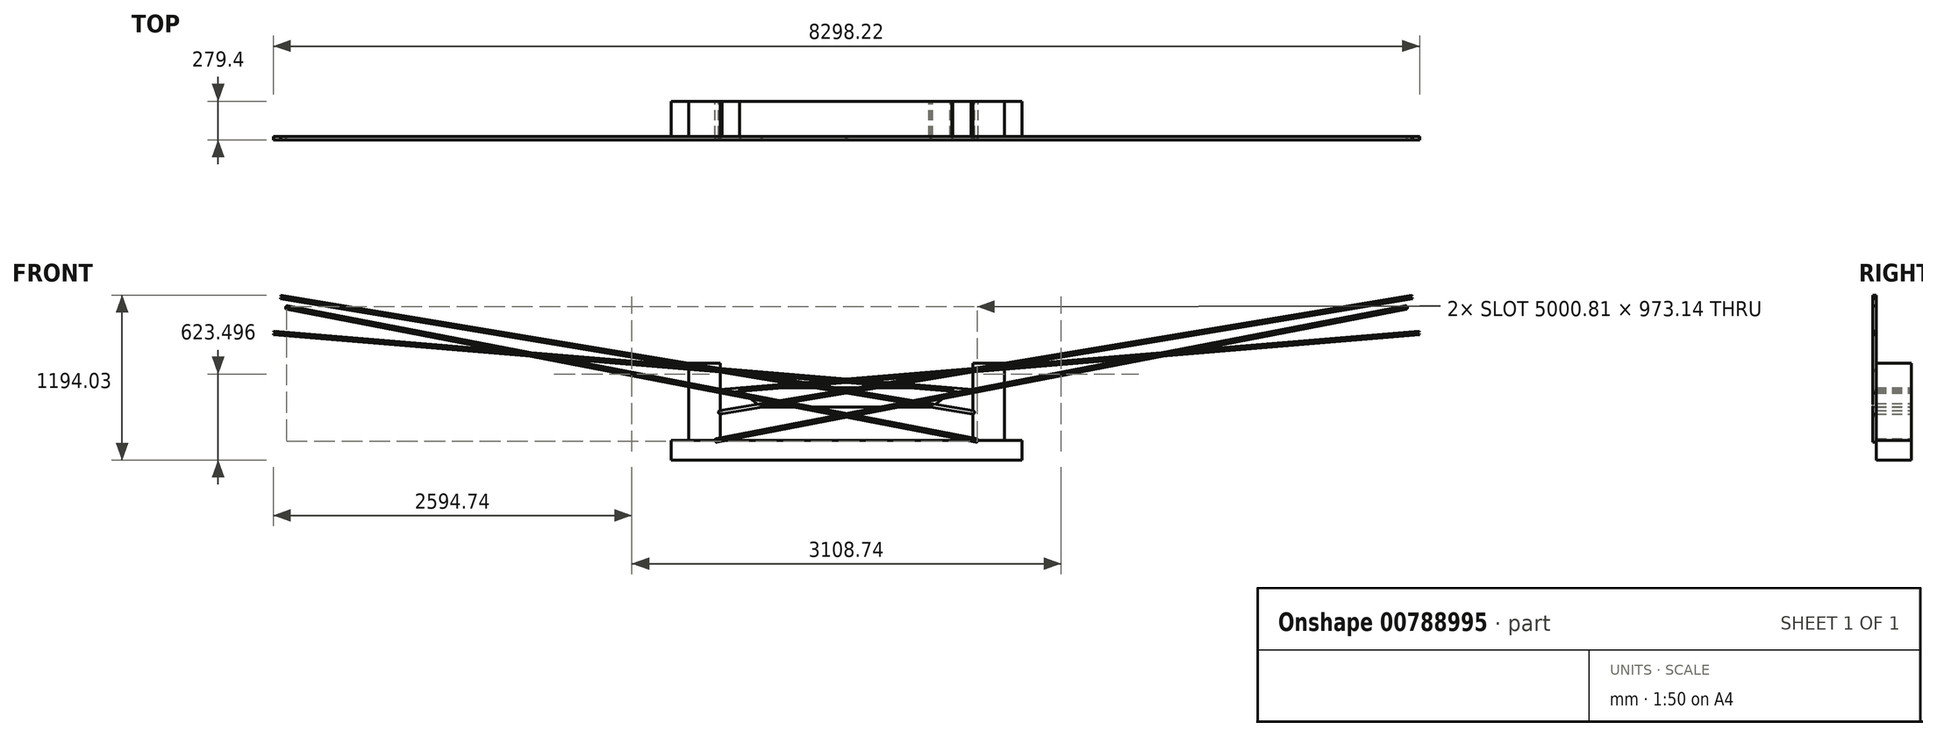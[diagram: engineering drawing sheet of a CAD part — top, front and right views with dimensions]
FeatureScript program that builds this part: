
annotation { "Feature Type Name" : "Feature", "Feature Type Description" : "" }
export const myFeature = defineFeature(function(context is Context, id is Id, definition is map)
    precondition{}
    {
        {
            var Q0;
            Q0=qCreatedBy(makeId("Front.planeOp"),FACE);
            var sketch = newSketch(context, id + "F0", { "sketchPlane" : qUnion([Q0])});
            skLineSegment(sketch, "E0.bottom", {"start": v(-914.4, 0) * mm, "end": v(-1143, 0) * mm});
            skLineSegment(sketch, "E0.top", {"start": v(-914.4, 558.8) * mm, "end": v(-1143, 558.8) * mm});
            skLineSegment(sketch, "E0.left", {"start": v(-914.4, 0) * mm, "end": v(-914.4, 558.8) * mm});
            skLineSegment(sketch, "E0.right", {"start": v(-1143, 0) * mm, "end": v(-1143, 558.8) * mm});
            skLineSegment(sketch, "E1.bottom", {"start": v(914.4, 0) * mm, "end": v(1143, 0) * mm});
            skLineSegment(sketch, "E1.top", {"start": v(914.4, 558.8) * mm, "end": v(1143, 558.8) * mm});
            skLineSegment(sketch, "E1.left", {"start": v(914.4, 0) * mm, "end": v(914.4, 558.8) * mm});
            skLineSegment(sketch, "E1.right", {"start": v(1143, 0) * mm, "end": v(1143, 558.8) * mm});
            skLineSegment(sketch, "E2", {"start": v(0, 0) * mm, "end": v(914.4, 0) * mm});
            skLineSegment(sketch, "E3", {"start": v(0, 0) * mm, "end": v(-914.4, 0) * mm});
            skLineSegment(sketch, "E4", {"start": v(-914.4, 279.4) * mm, "end": v(914.4, 279.4) * mm});
            skLineSegment(sketch, "E5", {"start": v(-762, 279.4) * mm, "end": v(-762, 368.3) * mm});
            skLineSegment(sketch, "E6", {"start": v(-609.6, 279.4) * mm, "end": v(-609.6, 254) * mm});
            skLineSegment(sketch, "E7", {"start": v(-914.4, 279.4) * mm, "end": v(-914.4, 355.6) * mm});
            skLineSegment(sketch, "E8", {"start": v(-914.4, 279.4) * mm, "end": v(-914.4, 203.2) * mm});
            skCircle(sketch, "E9", {"center": v(-914.4, 355.6) * mm, "radius": 12.7 * mm});
            skCircle(sketch, "E10", {"center": v(-914.4, 203.2) * mm, "radius": 12.7 * mm});
            skCircle(sketch, "E11", {"center": v(-762, 368.3) * mm, "radius": 12.7 * mm});
            skCircle(sketch, "E12", {"center": v(-609.6, 254) * mm, "radius": 12.7 * mm});
            skLineSegment(sketch, "E13", {"start": v(-762, 381) * mm, "end": v(0, 381) * mm});
            skLineSegment(sketch, "E14", {"start": v(0, 381) * mm, "end": v(0, 241.3) * mm});
            skLineSegment(sketch, "E15", {"start": v(0, 241.3) * mm, "end": v(-609.6, 241.3) * mm});
            skLineSegment(sketch, "E16", {"start": v(-769.62, 358.14) * mm, "end": v(-617.22, 243.84) * mm});
            skLineSegment(sketch, "E17.MirrorCS", {"start": v(0, 241.3) * mm, "end": v(609.6, 241.3) * mm});
            skCircle(sketch, "E18.MirrorC", {"center": v(609.6, 254) * mm, "radius": 12.7 * mm});
            skLineSegment(sketch, "E19.MirrorCS", {"start": v(769.62, 358.14) * mm, "end": v(617.22, 243.84) * mm});
            skLineSegment(sketch, "E20.MirrorCS", {"start": v(762, 381) * mm, "end": v(0, 381) * mm});
            skCircle(sketch, "E21.MirrorC", {"center": v(762, 368.3) * mm, "radius": 12.7 * mm});
            skCircle(sketch, "E22.MirrorC", {"center": v(914.4, 203.2) * mm, "radius": 12.7 * mm});
            skCircle(sketch, "E23.MirrorC", {"center": v(914.4, 355.6) * mm, "radius": 12.7 * mm});
            skCircle(sketch, "E24", {"center": v(-939.8, 0) * mm, "radius": 12.7 * mm});
            skCircle(sketch, "E25.MirrorC", {"center": v(939.8, 0) * mm, "radius": 12.7 * mm});
            skSolve(sketch);
        }
        {
            var Q0;
            {var subQ1=sQuery(id+"F0.wireOp",EDGE,"E0.bottom");Q0=makeQuery(id+"F0.imprint","IMPRINT",FACE,{"disambiguationData":[TD([[makeQuery(id+"F0.imprint","IMPRINT",EDGE,{"derivedFrom":subQ1}),-1.0]])]});}
            var Q1;
            {var subQ0=sQuery(id+"F0.wireOp",EDGE,"E7");var subQ1=sQuery(id+"F0.wireOp",EDGE,"E0.left");var subQ2=makeQuery(id+"F0.imprint","INTERSECT",VERTEX,{"derivedFrom":[subQ1,subQ0]});Q1=makeQuery(id+"F0.imprint","IMPRINT",FACE,{"disambiguationData":[TD([[makeQuery(id+"F0.imprint","IMPRINT",EDGE,{"disambiguationData":[TD([[subQ2,-1.0]])],"derivedFrom":subQ1}),-1.0]])]});}
            var Q2;
            {var subQ0=sQuery(id+"F0.wireOp",EDGE,"E7");var subQ1=sQuery(id+"F0.wireOp",EDGE,"E0.left");var subQ2=makeQuery(id+"F0.imprint","INTERSECT",VERTEX,{"derivedFrom":[subQ1,subQ0]});Q2=makeQuery(id+"F0.imprint","IMPRINT",FACE,{"disambiguationData":[TD([[makeQuery(id+"F0.imprint","IMPRINT",EDGE,{"disambiguationData":[TD([[subQ2,-1.0]])],"derivedFrom":subQ1}),1.0]])]});}
            var Q3;
            {var subQ0=sQuery(id+"F0.wireOp",EDGE,"E11");var subQ1=makeQuery(id+"F0.imprint","INTERSECT",VERTEX,{"derivedFrom":[subQ0,sQuery(id+"F0.wireOp",EDGE,"E13")]});Q3=makeQuery(id+"F0.imprint","IMPRINT",FACE,{"disambiguationData":[TD([[makeQuery(id+"F0.imprint","IMPRINT",EDGE,{"disambiguationData":[TD([[subQ1,-1.0]])],"derivedFrom":subQ0}),1.0]])]});}
            var Q4;
            {var subQ0=sQuery(id+"F0.wireOp",EDGE,"E13");Q4=makeQuery(id+"F0.imprint","IMPRINT",FACE,{"disambiguationData":[TD([[makeQuery(id+"F0.imprint","IMPRINT",EDGE,{"derivedFrom":subQ0}),-1.0]])]});}
            var Q5;
            {var subQ0=sQuery(id+"F0.wireOp",EDGE,"E16");var subQ1=sQuery(id+"F0.wireOp",EDGE,"E5");var subQ2=makeQuery(id+"F0.imprint","INTERSECT",VERTEX,{"derivedFrom":[subQ1,subQ0]});Q5=makeQuery(id+"F0.imprint","IMPRINT",FACE,{"disambiguationData":[TD([[makeQuery(id+"F0.imprint","IMPRINT",EDGE,{"disambiguationData":[TD([[subQ2,-1.0]])],"derivedFrom":subQ1}),1.0]])]});}
            var Q6;
            {var subQ0=sQuery(id+"F0.wireOp",EDGE,"E8");var subQ1=sQuery(id+"F0.wireOp",EDGE,"E0.left");var subQ2=makeQuery(id+"F0.imprint","INTERSECT",VERTEX,{"derivedFrom":[subQ1,subQ0]});Q6=makeQuery(id+"F0.imprint","IMPRINT",FACE,{"disambiguationData":[TD([[makeQuery(id+"F0.imprint","IMPRINT",EDGE,{"disambiguationData":[TD([[subQ2,1.0]])],"derivedFrom":subQ1}),1.0]])]});}
            var Q7;
            {var subQ0=sQuery(id+"F0.wireOp",EDGE,"E8");var subQ1=sQuery(id+"F0.wireOp",EDGE,"E0.left");var subQ2=makeQuery(id+"F0.imprint","INTERSECT",VERTEX,{"derivedFrom":[subQ1,subQ0]});Q7=makeQuery(id+"F0.imprint","IMPRINT",FACE,{"disambiguationData":[TD([[makeQuery(id+"F0.imprint","IMPRINT",EDGE,{"disambiguationData":[TD([[subQ2,1.0]])],"derivedFrom":subQ1}),-1.0]])]});}
            var Q8;
            {var subQ0=sQuery(id+"F0.wireOp",EDGE,"E6");var subQ1=sQuery(id+"F0.wireOp",EDGE,"E4");var subQ2=makeQuery(id+"F0.imprint","INTERSECT",VERTEX,{"derivedFrom":[subQ1,subQ0]});Q8=makeQuery(id+"F0.imprint","IMPRINT",FACE,{"disambiguationData":[TD([[makeQuery(id+"F0.imprint","IMPRINT",EDGE,{"disambiguationData":[TD([[subQ2,1.0]])],"derivedFrom":subQ1}),-1.0]])]});}
            var Q9;
            {var subQ0=sQuery(id+"F0.wireOp",EDGE,"E12");var subQ1=makeQuery(id+"F0.imprint","INTERSECT",VERTEX,{"derivedFrom":[subQ0,sQuery(id+"F0.wireOp",EDGE,"E16")]});Q9=makeQuery(id+"F0.imprint","IMPRINT",FACE,{"disambiguationData":[TD([[makeQuery(id+"F0.imprint","IMPRINT",EDGE,{"disambiguationData":[TD([[subQ1,1.0]])],"derivedFrom":subQ0}),1.0]])]});}
            var Q10;
            {var subQ0=sQuery(id+"F0.wireOp",EDGE,"E15");Q10=makeQuery(id+"F0.imprint","IMPRINT",FACE,{"disambiguationData":[TD([[makeQuery(id+"F0.imprint","IMPRINT",EDGE,{"derivedFrom":subQ0}),-1.0]])]});}
            var Q11;
            {var subQ1=sQuery(id+"F0.wireOp",EDGE,"E17.MirrorCS");Q11=makeQuery(id+"F0.imprint","IMPRINT",FACE,{"disambiguationData":[TD([[makeQuery(id+"F0.imprint","IMPRINT",EDGE,{"derivedFrom":subQ1}),1.0]])]});}
            var Q12;
            {var subQ0=sQuery(id+"F0.wireOp",EDGE,"E18.MirrorC");var subQ1=makeQuery(id+"F0.imprint","INTERSECT",VERTEX,{"derivedFrom":[sQuery(id+"F0.wireOp",EDGE,"E17.MirrorCS"),subQ0]});Q12=makeQuery(id+"F0.imprint","IMPRINT",FACE,{"disambiguationData":[TD([[makeQuery(id+"F0.imprint","IMPRINT",EDGE,{"disambiguationData":[TD([[subQ1,1.0]])],"derivedFrom":subQ0}),-1.0]])]});}
            var Q13;
            {var subQ0=sQuery(id+"F0.wireOp",EDGE,"E20.MirrorCS");Q13=makeQuery(id+"F0.imprint","IMPRINT",FACE,{"disambiguationData":[TD([[makeQuery(id+"F0.imprint","IMPRINT",EDGE,{"derivedFrom":subQ0}),1.0]])]});}
            var Q14;
            {var subQ0=sQuery(id+"F0.wireOp",EDGE,"E21.MirrorC");var subQ1=makeQuery(id+"F0.imprint","INTERSECT",VERTEX,{"derivedFrom":[sQuery(id+"F0.wireOp",EDGE,"E19.MirrorCS"),subQ0]});Q14=makeQuery(id+"F0.imprint","IMPRINT",FACE,{"disambiguationData":[TD([[makeQuery(id+"F0.imprint","IMPRINT",EDGE,{"disambiguationData":[TD([[subQ1,1.0]])],"derivedFrom":subQ0}),-1.0]])]});}
            var Q15;
            {var subQ0=sQuery(id+"F0.wireOp",EDGE,"E23.MirrorC");var subQ1=sQuery(id+"F0.wireOp",EDGE,"E1.left");var subQ2=makeQuery(id+"F0.imprint","INTERSECT",VERTEX,{"disambiguationData":[OD(0.0)],"derivedFrom":[subQ1,subQ0]});Q15=makeQuery(id+"F0.imprint","IMPRINT",FACE,{"disambiguationData":[TD([[makeQuery(id+"F0.imprint","IMPRINT",EDGE,{"disambiguationData":[TD([[subQ2,-1.0]])],"derivedFrom":subQ1}),-1.0]])]});}
            var Q16;
            {var subQ0=sQuery(id+"F0.wireOp",EDGE,"E23.MirrorC");var subQ1=sQuery(id+"F0.wireOp",EDGE,"E1.left");var subQ2=makeQuery(id+"F0.imprint","INTERSECT",VERTEX,{"disambiguationData":[OD(0.0)],"derivedFrom":[subQ1,subQ0]});Q16=makeQuery(id+"F0.imprint","IMPRINT",FACE,{"disambiguationData":[TD([[makeQuery(id+"F0.imprint","IMPRINT",EDGE,{"disambiguationData":[TD([[subQ2,-1.0]])],"derivedFrom":subQ1}),1.0]])]});}
            var Q17;
            {var subQ4=sQuery(id+"F0.wireOp",EDGE,"E1.bottom");Q17=makeQuery(id+"F0.imprint","IMPRINT",FACE,{"disambiguationData":[TD([[makeQuery(id+"F0.imprint","IMPRINT",EDGE,{"derivedFrom":subQ4}),1.0]])]});}
            var Q18;
            {var subQ0=sQuery(id+"F0.wireOp",EDGE,"E22.MirrorC");var subQ1=sQuery(id+"F0.wireOp",EDGE,"E1.left");var subQ2=makeQuery(id+"F0.imprint","INTERSECT",VERTEX,{"disambiguationData":[OD(0.0)],"derivedFrom":[subQ1,subQ0]});Q18=makeQuery(id+"F0.imprint","IMPRINT",FACE,{"disambiguationData":[TD([[makeQuery(id+"F0.imprint","IMPRINT",EDGE,{"disambiguationData":[TD([[subQ2,-1.0]])],"derivedFrom":subQ1}),-1.0]])]});}
            var Q19;
            {var subQ0=sQuery(id+"F0.wireOp",EDGE,"E22.MirrorC");var subQ1=sQuery(id+"F0.wireOp",EDGE,"E1.left");var subQ2=makeQuery(id+"F0.imprint","INTERSECT",VERTEX,{"disambiguationData":[OD(0.0)],"derivedFrom":[subQ1,subQ0]});Q19=makeQuery(id+"F0.imprint","IMPRINT",FACE,{"disambiguationData":[TD([[makeQuery(id+"F0.imprint","IMPRINT",EDGE,{"disambiguationData":[TD([[subQ2,-1.0]])],"derivedFrom":subQ1}),1.0]])]});}
            var Q20;
            {var subQ0=sQuery(id+"F0.wireOp",EDGE,"E24");var subQ1=sQuery(id+"F0.wireOp",EDGE,"E0.bottom");var subQ2=makeQuery(id+"F0.imprint","INTERSECT",VERTEX,{"disambiguationData":[OD(0.0)],"derivedFrom":[subQ1,subQ0]});Q20=makeQuery(id+"F0.imprint","IMPRINT",FACE,{"disambiguationData":[TD([[makeQuery(id+"F0.imprint","IMPRINT",EDGE,{"disambiguationData":[TD([[subQ2,-1.0]])],"derivedFrom":subQ1}),-1.0]])]});}
            var Q21;
            {var subQ0=sQuery(id+"F0.wireOp",EDGE,"E24");var subQ1=sQuery(id+"F0.wireOp",EDGE,"E0.bottom");var subQ2=makeQuery(id+"F0.imprint","INTERSECT",VERTEX,{"disambiguationData":[OD(0.0)],"derivedFrom":[subQ1,subQ0]});Q21=makeQuery(id+"F0.imprint","IMPRINT",FACE,{"disambiguationData":[TD([[makeQuery(id+"F0.imprint","IMPRINT",EDGE,{"disambiguationData":[TD([[subQ2,-1.0]])],"derivedFrom":subQ1}),1.0]])]});}
            var Q22;
            {var subQ0=sQuery(id+"F0.wireOp",EDGE,"E25.MirrorC");var subQ1=sQuery(id+"F0.wireOp",EDGE,"E1.bottom");var subQ2=makeQuery(id+"F0.imprint","INTERSECT",VERTEX,{"disambiguationData":[OD(0.0)],"derivedFrom":[subQ1,subQ0]});Q22=makeQuery(id+"F0.imprint","IMPRINT",FACE,{"disambiguationData":[TD([[makeQuery(id+"F0.imprint","IMPRINT",EDGE,{"disambiguationData":[TD([[subQ2,-1.0]])],"derivedFrom":subQ1}),1.0]])]});}
            var Q23;
            {var subQ0=sQuery(id+"F0.wireOp",EDGE,"E25.MirrorC");var subQ1=sQuery(id+"F0.wireOp",EDGE,"E1.bottom");var subQ2=makeQuery(id+"F0.imprint","INTERSECT",VERTEX,{"disambiguationData":[OD(0.0)],"derivedFrom":[subQ1,subQ0]});Q23=makeQuery(id+"F0.imprint","IMPRINT",FACE,{"disambiguationData":[TD([[makeQuery(id+"F0.imprint","IMPRINT",EDGE,{"disambiguationData":[TD([[subQ2,-1.0]])],"derivedFrom":subQ1}),-1.0]])]});}
            extrude(context, id + "F1", {"entities" : qUnion([Q0, Q1, Q2, Q3, Q4, Q5, Q6, Q7, Q8, Q9, Q10, Q11, Q12, Q13, Q14, Q15, Q16, Q17, Q18, Q19, Q20, Q21, Q22, Q23]), "depth" : 254 * mm, "offsetDistance" : 25.4 * mm});
        }
        {
            var Q0;
            Q0=makeQuery(id+"F1.opExtrude","CAP_FACE",FACE,{"disambiguationData":[OSD([sQuery(id+"F0.wireOp",EDGE,"E11"),sQuery(id+"F0.wireOp",EDGE,"E12"),sQuery(id+"F0.wireOp",EDGE,"E13"),sQuery(id+"F0.wireOp",EDGE,"E15"),sQuery(id+"F0.wireOp",EDGE,"E16"),sQuery(id+"F0.wireOp",EDGE,"E17.MirrorCS"),sQuery(id+"F0.wireOp",EDGE,"E18.MirrorC"),sQuery(id+"F0.wireOp",EDGE,"E19.MirrorCS"),sQuery(id+"F0.wireOp",EDGE,"E20.MirrorCS"),sQuery(id+"F0.wireOp",EDGE,"E21.MirrorC")])],"isStart":false});
            var sketch = newSketch(context, id + "F2", { "sketchPlane" : qUnion([Q0])});
            skCircle(sketch, "E26", {"center": v(-914.4, 355.6) * mm, "radius": 12.7 * mm});
            skCircle(sketch, "E27", {"center": v(-762, 368.3) * mm, "radius": 12.7 * mm});
            skLineSegment(sketch, "E28", {"start": v(-915.45, 368.26) * mm, "end": v(4147, 790.13) * mm});
            skLineSegment(sketch, "E29", {"start": v(4147, 790.13) * mm, "end": v(4149.1, 764.81) * mm});
            skLineSegment(sketch, "E30", {"start": v(4149.1, 764.81) * mm, "end": v(-913.35, 342.94) * mm});
            skArc(sketch, "E31", {"start": v(4147, 790.13) * mm, "mid": v(4160.7, 778.53) * mm, "end": v(4149.1, 764.81) * mm});
            skCircle(sketch, "E32", {"center": v(-762, 368.3) * mm, "radius": 6.35 * mm});
            skCircle(sketch, "E33", {"center": v(4148.05, 777.47) * mm, "radius": 6.35 * mm});
            skLineSegment(sketch, "E34", {"start": v(4148.58, 771.14) * mm, "end": v(-761.47, 361.97) * mm});
            skLineSegment(sketch, "E35", {"start": v(4147.53, 783.8) * mm, "end": v(-762.53, 374.63) * mm});
            skSolve(sketch);
        }
        {
            var Q0;
            {var subQ0=sQuery(id+"F2.wireOp",EDGE,"E28");var subQ1=sQuery(id+"F2.wireOp",EDGE,"E26");var subQ2=makeQuery(id+"F2.imprint","INTERSECT",VERTEX,{"derivedFrom":[subQ1,subQ0]});Q0=makeQuery(id+"F2.imprint","IMPRINT",FACE,{"disambiguationData":[TD([[makeQuery(id+"F2.imprint","IMPRINT",EDGE,{"disambiguationData":[TD([[subQ2,1.0]])],"derivedFrom":subQ1}),-1.0]])]});}
            var Q1;
            {var subQ0=sQuery(id+"F2.wireOp",EDGE,"E27");var subQ1=makeQuery(id+"F2.imprint","INTERSECT",VERTEX,{"derivedFrom":[makeQuery(id+"F1.opExtrude","CAP_EDGE",EDGE,{"disambiguationData":[OSD([sQuery(id+"F0.wireOp",EDGE,"E16")])],"isStart":false}),subQ0]});Q1=makeQuery(id+"F2.imprint","IMPRINT",FACE,{"disambiguationData":[TD([[makeQuery(id+"F2.imprint","IMPRINT",EDGE,{"disambiguationData":[TD([[subQ1,1.0]])],"derivedFrom":subQ0}),1.0]])]});}
            var Q2;
            {var subQ5=sQuery(id+"F2.wireOp",EDGE,"E27");var subQ7=sQuery(id+"F2.wireOp",EDGE,"E28");var subQ8=makeQuery(id+"F2.imprint","INTERSECT",VERTEX,{"derivedFrom":[subQ5,subQ7]});Q2=makeQuery(id+"F2.imprint","IMPRINT",FACE,{"disambiguationData":[TD([[makeQuery(id+"F2.imprint","IMPRINT",EDGE,{"disambiguationData":[TD([[subQ8,1.0]])],"derivedFrom":subQ5}),-1.0]])]});}
            var Q3;
            {var subQ0=sQuery(id+"F2.wireOp",EDGE,"E27");var subQ3=sQuery(id+"F2.wireOp",EDGE,"E35");var subQ4=makeQuery(id+"F2.imprint","INTERSECT",VERTEX,{"derivedFrom":[subQ0,subQ3]});Q3=makeQuery(id+"F2.imprint","IMPRINT",FACE,{"disambiguationData":[TD([[makeQuery(id+"F2.imprint","IMPRINT",EDGE,{"disambiguationData":[TD([[subQ4,-1.0]])],"derivedFrom":subQ0}),-1.0]])]});}
            var Q4;
            {var subQ0=sQuery(id+"F2.wireOp",EDGE,"E30");var subQ1=sQuery(id+"F2.wireOp",EDGE,"E27");var subQ2=makeQuery(id+"F2.imprint","INTERSECT",VERTEX,{"derivedFrom":[subQ1,subQ0]});Q4=makeQuery(id+"F2.imprint","IMPRINT",FACE,{"disambiguationData":[TD([[makeQuery(id+"F2.imprint","IMPRINT",EDGE,{"disambiguationData":[TD([[subQ2,-1.0]])],"derivedFrom":subQ1}),-1.0]])]});}
            var Q5;
            {var subQ0=sQuery(id+"F2.wireOp",EDGE,"E30");var subQ1=sQuery(id+"F2.wireOp",EDGE,"E29");var subQ2=makeQuery(id+"F2.imprint","INTERSECT",VERTEX,{"derivedFrom":[subQ1,subQ0,sQuery(id+"F2.wireOp",EDGE,"E31")]});Q5=makeQuery(id+"F2.imprint","IMPRINT",FACE,{"disambiguationData":[TD([[makeQuery(id+"F2.imprint","IMPRINT",EDGE,{"disambiguationData":[TD([[subQ2,1.0]])],"derivedFrom":subQ1}),-1.0]])]});}
            var Q6;
            {var subQ0=sQuery(id+"F2.wireOp",EDGE,"E31");Q6=makeQuery(id+"F2.imprint","IMPRINT",FACE,{"disambiguationData":[TD([[makeQuery(id+"F2.imprint","IMPRINT",EDGE,{"derivedFrom":subQ0}),-1.0]])]});}
            var Q7;
            {var subQ0=sQuery(id+"F2.wireOp",EDGE,"E26");var subQ1=makeQuery(id+"F2.imprint","INTERSECT",VERTEX,{"derivedFrom":[subQ0,sQuery(id+"F2.wireOp",EDGE,"E28")]});Q7=makeQuery(id+"F2.imprint","IMPRINT",FACE,{"disambiguationData":[TD([[makeQuery(id+"F2.imprint","IMPRINT",EDGE,{"disambiguationData":[TD([[subQ1,-1.0]])],"derivedFrom":subQ0}),1.0]])]});}
            extrude(context, id + "F3", {"entities" : qUnion([Q0, Q1, Q2, Q3, Q4, Q5, Q6, Q7]), "depth" : 25.4 * mm, "offsetDistance" : 25.4 * mm});
        }
        {
            var Q0;
            Q0=makeQuery(id+"F1.opExtrude","CAP_FACE",FACE,{"disambiguationData":[OSD([sQuery(id+"F0.wireOp",EDGE,"E11"),sQuery(id+"F0.wireOp",EDGE,"E12"),sQuery(id+"F0.wireOp",EDGE,"E13"),sQuery(id+"F0.wireOp",EDGE,"E15"),sQuery(id+"F0.wireOp",EDGE,"E16"),sQuery(id+"F0.wireOp",EDGE,"E17.MirrorCS"),sQuery(id+"F0.wireOp",EDGE,"E18.MirrorC"),sQuery(id+"F0.wireOp",EDGE,"E19.MirrorCS"),sQuery(id+"F0.wireOp",EDGE,"E20.MirrorCS"),sQuery(id+"F0.wireOp",EDGE,"E21.MirrorC")])],"isStart":false});
            var sketch = newSketch(context, id + "F4", { "sketchPlane" : qUnion([Q0])});
            skCircle(sketch, "E36", {"center": v(-914.4, 203.2) * mm, "radius": 12.7 * mm});
            skCircle(sketch, "E37", {"center": v(-609.6, 254) * mm, "radius": 12.7 * mm});
            skLineSegment(sketch, "E38", {"start": v(-916.49, 215.73) * mm, "end": v(4094.4, 1050.87) * mm});
            skLineSegment(sketch, "E39", {"start": v(4094.4, 1050.87) * mm, "end": v(4098.57, 1025.82) * mm});
            skLineSegment(sketch, "E40", {"start": v(4098.57, 1025.82) * mm, "end": v(-912.31, 190.67) * mm});
            skArc(sketch, "E41", {"start": v(4094.4, 1050.87) * mm, "mid": v(4109, 1040.43) * mm, "end": v(4098.57, 1025.82) * mm});
            skCircle(sketch, "E42", {"center": v(-609.6, 254) * mm, "radius": 6.35 * mm});
            skCircle(sketch, "E43", {"center": v(4096.48, 1038.35) * mm, "radius": 6.35 * mm});
            skLineSegment(sketch, "E44", {"start": v(4095.44, 1044.61) * mm, "end": v(-610.64, 260.26) * mm});
            skLineSegment(sketch, "E45", {"start": v(4097.53, 1032.08) * mm, "end": v(-608.56, 247.74) * mm});
            skSolve(sketch);
        }
        {
            var Q0;
            {var subQ0=sQuery(id+"F4.wireOp",EDGE,"E41");Q0=makeQuery(id+"F4.imprint","IMPRINT",FACE,{"disambiguationData":[TD([[makeQuery(id+"F4.imprint","IMPRINT",EDGE,{"derivedFrom":subQ0}),-1.0]])]});}
            var Q1;
            {var subQ0=sQuery(id+"F4.wireOp",EDGE,"E40");var subQ1=sQuery(id+"F4.wireOp",EDGE,"E37");var subQ2=makeQuery(id+"F4.imprint","INTERSECT",VERTEX,{"derivedFrom":[subQ1,subQ0]});Q1=makeQuery(id+"F4.imprint","IMPRINT",FACE,{"disambiguationData":[TD([[makeQuery(id+"F4.imprint","IMPRINT",EDGE,{"disambiguationData":[TD([[subQ2,-1.0]])],"derivedFrom":subQ1}),-1.0]])]});}
            var Q2;
            {var subQ0=sQuery(id+"F4.wireOp",EDGE,"E38");var subQ1=sQuery(id+"F4.wireOp",EDGE,"E37");var subQ2=makeQuery(id+"F4.imprint","INTERSECT",VERTEX,{"derivedFrom":[subQ1,subQ0]});Q2=makeQuery(id+"F4.imprint","IMPRINT",FACE,{"disambiguationData":[TD([[makeQuery(id+"F4.imprint","IMPRINT",EDGE,{"disambiguationData":[TD([[subQ2,1.0]])],"derivedFrom":subQ1}),-1.0]])]});}
            var Q3;
            {var subQ0=sQuery(id+"F4.wireOp",EDGE,"E37");var subQ1=makeQuery(id+"F1.opExtrude","CAP_EDGE",EDGE,{"disambiguationData":[OSD([sQuery(id+"F0.wireOp",EDGE,"E16")])],"isStart":false});var subQ2=makeQuery(id+"F4.imprint","INTERSECT",VERTEX,{"derivedFrom":[subQ1,subQ0]});Q3=makeQuery(id+"F4.imprint","IMPRINT",FACE,{"disambiguationData":[TD([[makeQuery(id+"F4.imprint","IMPRINT",EDGE,{"disambiguationData":[TD([[subQ2,1.0]])],"derivedFrom":subQ0}),-1.0]])]});}
            var Q4;
            {var subQ0=sQuery(id+"F4.wireOp",EDGE,"E38");var subQ1=sQuery(id+"F4.wireOp",EDGE,"E36");var subQ2=makeQuery(id+"F4.imprint","INTERSECT",VERTEX,{"derivedFrom":[subQ1,subQ0]});Q4=makeQuery(id+"F4.imprint","IMPRINT",FACE,{"disambiguationData":[TD([[makeQuery(id+"F4.imprint","IMPRINT",EDGE,{"disambiguationData":[TD([[subQ2,1.0]])],"derivedFrom":subQ1}),-1.0]])]});}
            var Q5;
            {var subQ0=sQuery(id+"F4.wireOp",EDGE,"E37");var subQ4=makeQuery(id+"F4.imprint","INTERSECT",VERTEX,{"derivedFrom":[subQ0,sQuery(id+"F4.wireOp",EDGE,"E38")]});Q5=makeQuery(id+"F4.imprint","IMPRINT",FACE,{"disambiguationData":[TD([[makeQuery(id+"F4.imprint","IMPRINT",EDGE,{"disambiguationData":[TD([[subQ4,1.0]])],"derivedFrom":subQ0}),1.0]])]});}
            var Q6;
            {var subQ0=sQuery(id+"F4.wireOp",EDGE,"E36");var subQ1=makeQuery(id+"F4.imprint","INTERSECT",VERTEX,{"derivedFrom":[subQ0,sQuery(id+"F4.wireOp",EDGE,"E38")]});Q6=makeQuery(id+"F4.imprint","IMPRINT",FACE,{"disambiguationData":[TD([[makeQuery(id+"F4.imprint","IMPRINT",EDGE,{"disambiguationData":[TD([[subQ1,-1.0]])],"derivedFrom":subQ0}),1.0]])]});}
            var Q7;
            {var subQ0=sQuery(id+"F4.wireOp",EDGE,"E39");var subQ1=sQuery(id+"F4.wireOp",EDGE,"E38");var subQ2=makeQuery(id+"F4.imprint","INTERSECT",VERTEX,{"derivedFrom":[subQ1,subQ0,sQuery(id+"F4.wireOp",EDGE,"E41")]});Q7=makeQuery(id+"F4.imprint","IMPRINT",FACE,{"disambiguationData":[TD([[makeQuery(id+"F4.imprint","IMPRINT",EDGE,{"disambiguationData":[TD([[subQ2,1.0]])],"derivedFrom":subQ1}),-1.0]])]});}
            var Q8;
            {var subQ0=sQuery(id+"F4.wireOp",EDGE,"E40");var subQ1=sQuery(id+"F4.wireOp",EDGE,"E39");var subQ2=makeQuery(id+"F4.imprint","INTERSECT",VERTEX,{"derivedFrom":[subQ1,subQ0,sQuery(id+"F4.wireOp",EDGE,"E41")]});Q8=makeQuery(id+"F4.imprint","IMPRINT",FACE,{"disambiguationData":[TD([[makeQuery(id+"F4.imprint","IMPRINT",EDGE,{"disambiguationData":[TD([[subQ2,1.0]])],"derivedFrom":subQ1}),-1.0]])]});}
            extrude(context, id + "F5", {"entities" : qUnion([Q0, Q1, Q2, Q3, Q4, Q5, Q6, Q7, Q8]), "depth" : 25.4 * mm, "offsetDistance" : 25.4 * mm});
        }
        {
            var Q0;
            Q0=makeQuery(id+"F1.opExtrude","CAP_FACE",FACE,{"disambiguationData":[OSD([sQuery(id+"F0.wireOp",EDGE,"E0.bottom"),sQuery(id+"F0.wireOp",EDGE,"E0.top"),sQuery(id+"F0.wireOp",EDGE,"E0.left"),sQuery(id+"F0.wireOp",EDGE,"E0.right"),sQuery(id+"F0.wireOp",EDGE,"E7"),sQuery(id+"F0.wireOp",EDGE,"E8"),sQuery(id+"F0.wireOp",EDGE,"E9"),sQuery(id+"F0.wireOp",EDGE,"E10")])],"isStart":false});
            var sketch = newSketch(context, id + "F6", { "sketchPlane" : qUnion([Q0])});
            skCircle(sketch, "E46", {"center": v(-939.8, 0) * mm, "radius": 12.7 * mm});
            skCircle(sketch, "E47", {"center": v(4048.54, 960.67) * mm, "radius": 12.7 * mm});
            skCircle(sketch, "E48", {"center": v(4048.54, 960.67) * mm, "radius": 6.35 * mm});
            skCircle(sketch, "E49", {"center": v(-939.8, 0) * mm, "radius": 6.35 * mm});
            skLineSegment(sketch, "E50", {"start": v(4046.14, 973.14) * mm, "end": v(-942.2, 12.47) * mm});
            skLineSegment(sketch, "E51", {"start": v(-937.4, -12.47) * mm, "end": v(4050.94, 948.2) * mm});
            skLineSegment(sketch, "E52", {"start": v(-941, 6.24) * mm, "end": v(4047.34, 966.9) * mm});
            skLineSegment(sketch, "E53", {"start": v(-938.6, -6.24) * mm, "end": v(4049.74, 954.44) * mm});
            skSolve(sketch);
        }
        {
            var Q0;
            {var subQ5=sQuery(id+"F6.wireOp",EDGE,"E46");var subQ6=makeQuery(id+"F6.imprint","INTERSECT",VERTEX,{"derivedFrom":[subQ5,sQuery(id+"F6.wireOp",EDGE,"E51")]});Q0=makeQuery(id+"F6.imprint","IMPRINT",FACE,{"disambiguationData":[TD([[makeQuery(id+"F6.imprint","IMPRINT",EDGE,{"disambiguationData":[TD([[subQ6,1.0]])],"derivedFrom":subQ5}),1.0]])]});}
            var Q1;
            {var subQ9=sQuery(id+"F6.wireOp",EDGE,"E46");var subQ10=makeQuery(id+"F6.imprint","INTERSECT",VERTEX,{"derivedFrom":[subQ9,sQuery(id+"F6.wireOp",EDGE,"E50")]});Q1=makeQuery(id+"F6.imprint","IMPRINT",FACE,{"disambiguationData":[TD([[makeQuery(id+"F6.imprint","IMPRINT",EDGE,{"disambiguationData":[TD([[subQ10,-1.0]])],"derivedFrom":subQ9}),1.0]])]});}
            var Q2;
            {var subQ0=sQuery(id+"F6.wireOp",EDGE,"E52");var subQ1=sQuery(id+"F6.wireOp",EDGE,"E46");var subQ2=makeQuery(id+"F6.imprint","INTERSECT",VERTEX,{"derivedFrom":[subQ1,subQ0]});Q2=makeQuery(id+"F6.imprint","IMPRINT",FACE,{"disambiguationData":[TD([[makeQuery(id+"F6.imprint","IMPRINT",EDGE,{"disambiguationData":[TD([[subQ2,-1.0]])],"derivedFrom":subQ1}),1.0]])]});}
            var Q3;
            {var subQ3=sQuery(id+"F6.wireOp",EDGE,"E47");var subQ5=sQuery(id+"F6.wireOp",EDGE,"E50");var subQ6=makeQuery(id+"F6.imprint","INTERSECT",VERTEX,{"derivedFrom":[subQ3,subQ5]});Q3=makeQuery(id+"F6.imprint","IMPRINT",FACE,{"disambiguationData":[TD([[makeQuery(id+"F6.imprint","IMPRINT",EDGE,{"disambiguationData":[TD([[subQ6,-1.0]])],"derivedFrom":subQ3}),-1.0]])]});}
            var Q4;
            {var subQ0=sQuery(id+"F6.wireOp",EDGE,"E51");Q4=makeQuery(id+"F6.imprint","IMPRINT",FACE,{"disambiguationData":[TD([[makeQuery(id+"F6.imprint","IMPRINT",EDGE,{"derivedFrom":subQ0}),1.0]])]});}
            var Q5;
            {var subQ0=sQuery(id+"F6.wireOp",EDGE,"E47");var subQ1=makeQuery(id+"F6.imprint","INTERSECT",VERTEX,{"derivedFrom":[subQ0,sQuery(id+"F6.wireOp",EDGE,"E50")]});Q5=makeQuery(id+"F6.imprint","IMPRINT",FACE,{"disambiguationData":[TD([[makeQuery(id+"F6.imprint","IMPRINT",EDGE,{"disambiguationData":[TD([[subQ1,-1.0]])],"derivedFrom":subQ0}),1.0]])]});}
            var Q6;
            {var subQ0=sQuery(id+"F6.wireOp",EDGE,"E50");var subQ1=sQuery(id+"F6.wireOp",EDGE,"E46");var subQ2=makeQuery(id+"F6.imprint","INTERSECT",VERTEX,{"derivedFrom":[subQ1,subQ0]});Q6=makeQuery(id+"F6.imprint","IMPRINT",FACE,{"disambiguationData":[TD([[makeQuery(id+"F6.imprint","IMPRINT",EDGE,{"disambiguationData":[TD([[subQ2,1.0]])],"derivedFrom":subQ1}),-1.0]])]});}
            extrude(context, id + "F7", {"entities" : qUnion([Q0, Q1, Q2, Q3, Q4, Q5, Q6]), "depth" : 25.4 * mm, "offsetDistance" : 25.4 * mm});
        }
        {
            var Q0;
            Q0=makeQuery(id+"F1.opExtrude","CAP_FACE",FACE,{"disambiguationData":[OSD([sQuery(id+"F0.wireOp",EDGE,"E1.bottom"),sQuery(id+"F0.wireOp",EDGE,"E1.top"),sQuery(id+"F0.wireOp",EDGE,"E1.left"),sQuery(id+"F0.wireOp",EDGE,"E1.right"),sQuery(id+"F0.wireOp",EDGE,"E22.MirrorC"),sQuery(id+"F0.wireOp",EDGE,"E23.MirrorC")])],"isStart":false});
            var sketch = newSketch(context, id + "F8", { "sketchPlane" : qUnion([Q0])});
            skCircle(sketch, "E54", {"center": v(914.4, 508) * mm, "radius": 6.35 * mm});
            skSolve(sketch);
        }
        {
            var Q0;
            {var subQ0=sQuery(id+"F8.wireOp",EDGE,"E54");var subQ1=sQuery(id+"F0.wireOp",EDGE,"E1.left");var subQ2=makeQuery(id+"F1.opExtrude","CAP_EDGE",EDGE,{"disambiguationData":[OSD([subQ1]),TDD([makeQuery(id+"F0.imprint","IMPRINT",EDGE,{"disambiguationData":[TD([[makeQuery(id+"F0.imprint","INTERSECT",VERTEX,{"derivedFrom":[sQuery(id+"F0.wireOp",EDGE,"E1.top"),subQ1]}),1.0]])],"derivedFrom":subQ1})])],"isStart":false});var subQ3=makeQuery(id+"F8.imprint","INTERSECT",VERTEX,{"disambiguationData":[OD(0.0)],"derivedFrom":[subQ2,subQ0]});Q0=makeQuery(id+"F8.imprint","IMPRINT",FACE,{"disambiguationData":[TD([[makeQuery(id+"F8.imprint","IMPRINT",EDGE,{"disambiguationData":[TD([[subQ3,-1.0]])],"derivedFrom":subQ0}),1.0]])]});}
            var Q1;
            {var subQ0=sQuery(id+"F8.wireOp",EDGE,"E54");var subQ1=sQuery(id+"F0.wireOp",EDGE,"E1.left");var subQ2=makeQuery(id+"F1.opExtrude","CAP_EDGE",EDGE,{"disambiguationData":[OSD([subQ1]),TDD([makeQuery(id+"F0.imprint","IMPRINT",EDGE,{"disambiguationData":[TD([[makeQuery(id+"F0.imprint","INTERSECT",VERTEX,{"derivedFrom":[sQuery(id+"F0.wireOp",EDGE,"E1.top"),subQ1]}),1.0]])],"derivedFrom":subQ1})])],"isStart":false});var subQ3=makeQuery(id+"F8.imprint","INTERSECT",VERTEX,{"disambiguationData":[OD(0.0)],"derivedFrom":[subQ2,subQ0]});Q1=makeQuery(id+"F8.imprint","IMPRINT",FACE,{"disambiguationData":[TD([[makeQuery(id+"F8.imprint","IMPRINT",EDGE,{"disambiguationData":[TD([[subQ3,1.0]])],"derivedFrom":subQ0}),1.0]])]});}
            extrude(context, id + "F9", {"entities" : qUnion([Q0, Q1]), "depth" : 25.4 * mm, "offsetDistance" : 25.4 * mm});
        }
        {
            var Q0;
            Q0=makeQuery(id+"F3.opExtrude","SWEPT_BODY",BODY,{"disambiguationData":[OSD([sQuery(id+"F0.wireOp",EDGE,"E16"),sQuery(id+"F2.wireOp",EDGE,"E26"),sQuery(id+"F2.wireOp",EDGE,"E27"),sQuery(id+"F2.wireOp",EDGE,"E28"),sQuery(id+"F2.wireOp",EDGE,"E30"),sQuery(id+"F2.wireOp",EDGE,"E31"),sQuery(id+"F2.wireOp",EDGE,"E32"),sQuery(id+"F2.wireOp",EDGE,"E33"),sQuery(id+"F2.wireOp",EDGE,"E34"),sQuery(id+"F2.wireOp",EDGE,"E35")])]});
            var Q1;
            Q1=makeQuery(id+"F5.opExtrude","SWEPT_BODY",BODY,{"disambiguationData":[OSD([sQuery(id+"F0.wireOp",EDGE,"E15"),sQuery(id+"F0.wireOp",EDGE,"E17.MirrorCS"),sQuery(id+"F4.wireOp",EDGE,"E36"),sQuery(id+"F4.wireOp",EDGE,"E37"),sQuery(id+"F4.wireOp",EDGE,"E38"),sQuery(id+"F4.wireOp",EDGE,"E40"),sQuery(id+"F4.wireOp",EDGE,"E41"),sQuery(id+"F4.wireOp",EDGE,"E42"),sQuery(id+"F4.wireOp",EDGE,"E43"),sQuery(id+"F4.wireOp",EDGE,"E44"),sQuery(id+"F4.wireOp",EDGE,"E45")])]});
            var Q2;
            Q2=makeQuery(id+"F7.opExtrude","SWEPT_BODY",BODY,{"disambiguationData":[OSD([sQuery(id+"F6.wireOp",EDGE,"E46"),sQuery(id+"F6.wireOp",EDGE,"E47"),sQuery(id+"F6.wireOp",EDGE,"E48"),sQuery(id+"F6.wireOp",EDGE,"E49"),sQuery(id+"F6.wireOp",EDGE,"E50"),sQuery(id+"F6.wireOp",EDGE,"E51"),sQuery(id+"F6.wireOp",EDGE,"E52"),sQuery(id+"F6.wireOp",EDGE,"E53")])]});
            var Q3;
            Q3=makeQuery(id+"F9.opExtrude","SWEPT_BODY",BODY,{"disambiguationData":[OSD([sQuery(id+"F8.wireOp",EDGE,"E54")])]});
            var Q4;
            Q4=qCreatedBy(makeId("Right.planeOp"),FACE);
            mirror(context, id + "F10", {"entities" : qUnion([Q0, Q1, Q2, Q3]), "mirrorPlane" : qUnion([Q4])});
        }
        {
            var Q0;
            Q0=makeQuery(id+"F1.opExtrude","CAP_FACE",FACE,{"disambiguationData":[OSD([sQuery(id+"F0.wireOp",EDGE,"E11"),sQuery(id+"F0.wireOp",EDGE,"E12"),sQuery(id+"F0.wireOp",EDGE,"E13"),sQuery(id+"F0.wireOp",EDGE,"E15"),sQuery(id+"F0.wireOp",EDGE,"E16"),sQuery(id+"F0.wireOp",EDGE,"E17.MirrorCS"),sQuery(id+"F0.wireOp",EDGE,"E18.MirrorC"),sQuery(id+"F0.wireOp",EDGE,"E19.MirrorCS"),sQuery(id+"F0.wireOp",EDGE,"E20.MirrorCS"),sQuery(id+"F0.wireOp",EDGE,"E21.MirrorC")])],"isStart":false});
            var sketch = newSketch(context, id + "F11", { "sketchPlane" : qUnion([Q0])});
            skCircle(sketch, "E55", {"center": v(0, 181) * mm, "radius": 6.35 * mm});
            skSolve(sketch);
        }
        {
            var Q0;
            Q0 = qSketchRegion(id + "F11", true);
            extrude(context, id + "F12", {"entities" : qUnion([Q0]), "depth" : 25.4 * mm, "offsetDistance" : 25.4 * mm});
        }
        {
            var Q0;
            Q0=makeQuery(id+"F1.opExtrude","CAP_FACE",FACE,{"disambiguationData":[OSD([sQuery(id+"F0.wireOp",EDGE,"E0.bottom"),sQuery(id+"F0.wireOp",EDGE,"E0.top"),sQuery(id+"F0.wireOp",EDGE,"E0.left"),sQuery(id+"F0.wireOp",EDGE,"E0.right"),sQuery(id+"F0.wireOp",EDGE,"E7"),sQuery(id+"F0.wireOp",EDGE,"E8"),sQuery(id+"F0.wireOp",EDGE,"E9"),sQuery(id+"F0.wireOp",EDGE,"E10"),sQuery(id+"F0.wireOp",EDGE,"E24")])],"isStart":false});
            var sketch = newSketch(context, id + "F13", { "sketchPlane" : qUnion([Q0])});
            skLineSegment(sketch, "E56.bottom", {"start": v(-1270, -143.16) * mm, "end": v(1270, -143.16) * mm});
            skLineSegment(sketch, "E56.top", {"start": v(-1270, 0) * mm, "end": v(1270, 0) * mm});
            skLineSegment(sketch, "E56.left", {"start": v(-1270, -143.16) * mm, "end": v(-1270, 0) * mm});
            skLineSegment(sketch, "E56.right", {"start": v(1270, -143.16) * mm, "end": v(1270, 0) * mm});
            skSolve(sketch);
        }
        {
            var Q0;
            Q0 = qSketchRegion(id + "F13", true);
            var Q1;
            Q1=makeQuery(id+"F1.opExtrude","CAP_FACE",FACE,{"disambiguationData":[OSD([sQuery(id+"F0.wireOp",EDGE,"E1.bottom"),sQuery(id+"F0.wireOp",EDGE,"E1.top"),sQuery(id+"F0.wireOp",EDGE,"E1.left"),sQuery(id+"F0.wireOp",EDGE,"E1.right"),sQuery(id+"F0.wireOp",EDGE,"E22.MirrorC"),sQuery(id+"F0.wireOp",EDGE,"E23.MirrorC"),sQuery(id+"F0.wireOp",EDGE,"E25.MirrorC")])],"isStart":true});
            extrude(context, id + "F14", {"entities" : qUnion([Q0]), "endBound" : BoundingType.UP_TO_SURFACE, "oppositeDirection" : true, "depth" : 25.4 * mm, "endBoundEntityFace" : qUnion([Q1]), "offsetDistance" : 25.4 * mm});
        }
    });
